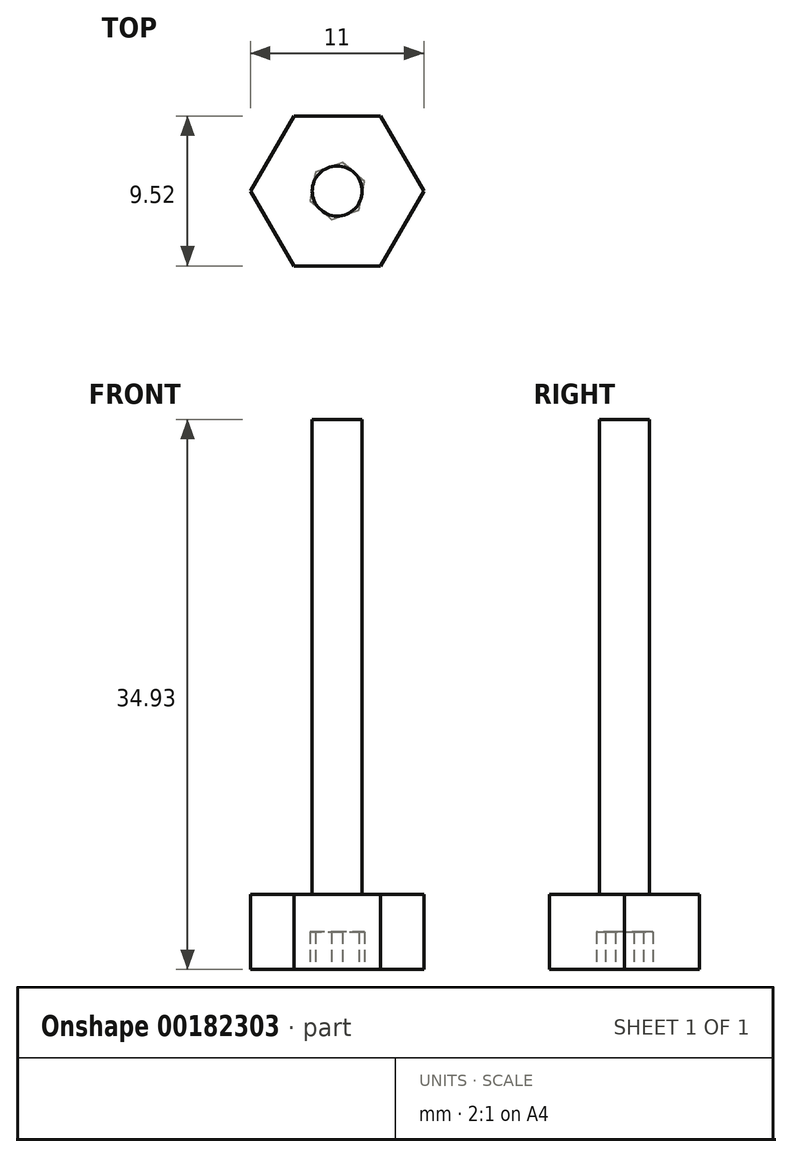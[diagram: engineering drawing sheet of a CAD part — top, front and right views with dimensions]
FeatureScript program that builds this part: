
annotation { "Feature Type Name" : "Feature", "Feature Type Description" : "" }
export const myFeature = defineFeature(function(context is Context, id is Id, definition is map)
    precondition{}
    {
        {
            var Q0;
            Q0=qCreatedBy(makeId("Top.planeOp"),FACE);
            var sketch = newSketch(context, id + "F0", { "sketchPlane" : qUnion([Q0])});
            skCircle(sketch, "E0.cCircle", {"center": v(0, 0) * mm, "radius": 4.76 * mm, "construction": true});
            skLineSegment(sketch, "E0.0", {"start": v(-2.75, 4.76) * mm, "end": v(2.75, 4.76) * mm});
            skLineSegment(sketch, "E0.1", {"start": v(2.75, 4.76) * mm, "end": v(5.5, 0) * mm});
            skLineSegment(sketch, "E0.2", {"start": v(5.5, 0) * mm, "end": v(2.75, -4.76) * mm});
            skLineSegment(sketch, "E0.3", {"start": v(2.75, -4.76) * mm, "end": v(-2.75, -4.76) * mm});
            skLineSegment(sketch, "E0.4", {"start": v(-2.75, -4.76) * mm, "end": v(-5.5, 0) * mm});
            skLineSegment(sketch, "E0.5", {"start": v(-5.5, 0) * mm, "end": v(-2.75, 4.76) * mm});
            skPoint(sketch, "E0.0.midPoint", {"position": v(0, 4.76) * mm});
            skCircle(sketch, "E1", {"center": v(0, 0) * mm, "radius": 1.59 * mm});
            skSolve(sketch);
        }
        {
            var Q0;
            Q0 = qSketchRegion(id + "F0", true);
            extrude(context, id + "F1", {"entities" : qUnion([Q0]), "depth" : 4.76 * mm});
        }
        {
            var Q0;
            Q0=makeQuery(id+"F0.imprint","IMPRINT",FACE,{"disambiguationData":[TD([[makeQuery(id+"F0.imprint","IMPRINT",EDGE,{"derivedFrom":sQuery(id+"F0.wireOp",EDGE,"E1")}),1.0]])]});
            extrude(context, id + "F2", {"entities" : qUnion([Q0]), "operationType" : NewBodyOperationType.REMOVE, "depth" : 4.76 * mm});
        }
        {
            var Q0;
            Q0=qCreatedBy(makeId("Top.planeOp"),FACE);
            var sketch = newSketch(context, id + "F3", { "sketchPlane" : qUnion([Q0])});
            skCircle(sketch, "E2", {"center": v(0, 0) * mm, "radius": 3.18 * mm});
            skSolve(sketch);
        }
        {
            var Q0;
            Q0 = qSketchRegion(id + "F3", true);
            extrude(context, id + "F4", {"entities" : qUnion([Q0]), "depth" : 3.17 * mm});
        }
        {
            var Q0;
            Q0=qCreatedBy(makeId("Top.planeOp"),FACE);
            var sketch = newSketch(context, id + "F5", { "sketchPlane" : qUnion([Q0])});
            skCircle(sketch, "E3", {"center": v(0, 0) * mm, "radius": 1.59 * mm});
            skSolve(sketch);
        }
        {
            var Q0;
            Q0 = qSketchRegion(id + "F5", true);
            extrude(context, id + "F6", {"entities" : qUnion([Q0]), "operationType" : NewBodyOperationType.ADD, "depth" : 34.92 * mm});
        }
        {
            var Q0;
            Q0=makeQuery(id+"F4.opExtrude","CAP_FACE",FACE,{"disambiguationData":[OSD([sQuery(id+"F3.wireOp",EDGE,"E2")])],"isStart":true});
            var sketch = newSketch(context, id + "F7", { "sketchPlane" : qUnion([Q0])});
            skCircle(sketch, "E4.cCircle", {"center": v(0, 0) * mm, "radius": 1.59 * mm, "construction": true});
            skLineSegment(sketch, "E4.0", {"start": v(-1.73, 0.6) * mm, "end": v(-0.35, 1.8) * mm});
            skLineSegment(sketch, "E4.1", {"start": v(-0.35, 1.8) * mm, "end": v(1.38, 1.2) * mm});
            skLineSegment(sketch, "E4.2", {"start": v(1.38, 1.2) * mm, "end": v(1.73, -0.6) * mm});
            skLineSegment(sketch, "E4.3", {"start": v(1.73, -0.6) * mm, "end": v(0.35, -1.8) * mm});
            skLineSegment(sketch, "E4.4", {"start": v(0.35, -1.8) * mm, "end": v(-1.38, -1.2) * mm});
            skLineSegment(sketch, "E4.5", {"start": v(-1.38, -1.2) * mm, "end": v(-1.73, 0.6) * mm});
            skPoint(sketch, "E4.0.midPoint", {"position": v(-1.04, 1.2) * mm});
            skSolve(sketch);
        }
        {
            var Q0;
            Q0 = qSketchRegion(id + "F7", true);
            extrude(context, id + "F8", {"entities" : qUnion([Q0]), "operationType" : NewBodyOperationType.REMOVE, "oppositeDirection" : true, "depth" : 2.38 * mm});
        }
    });
